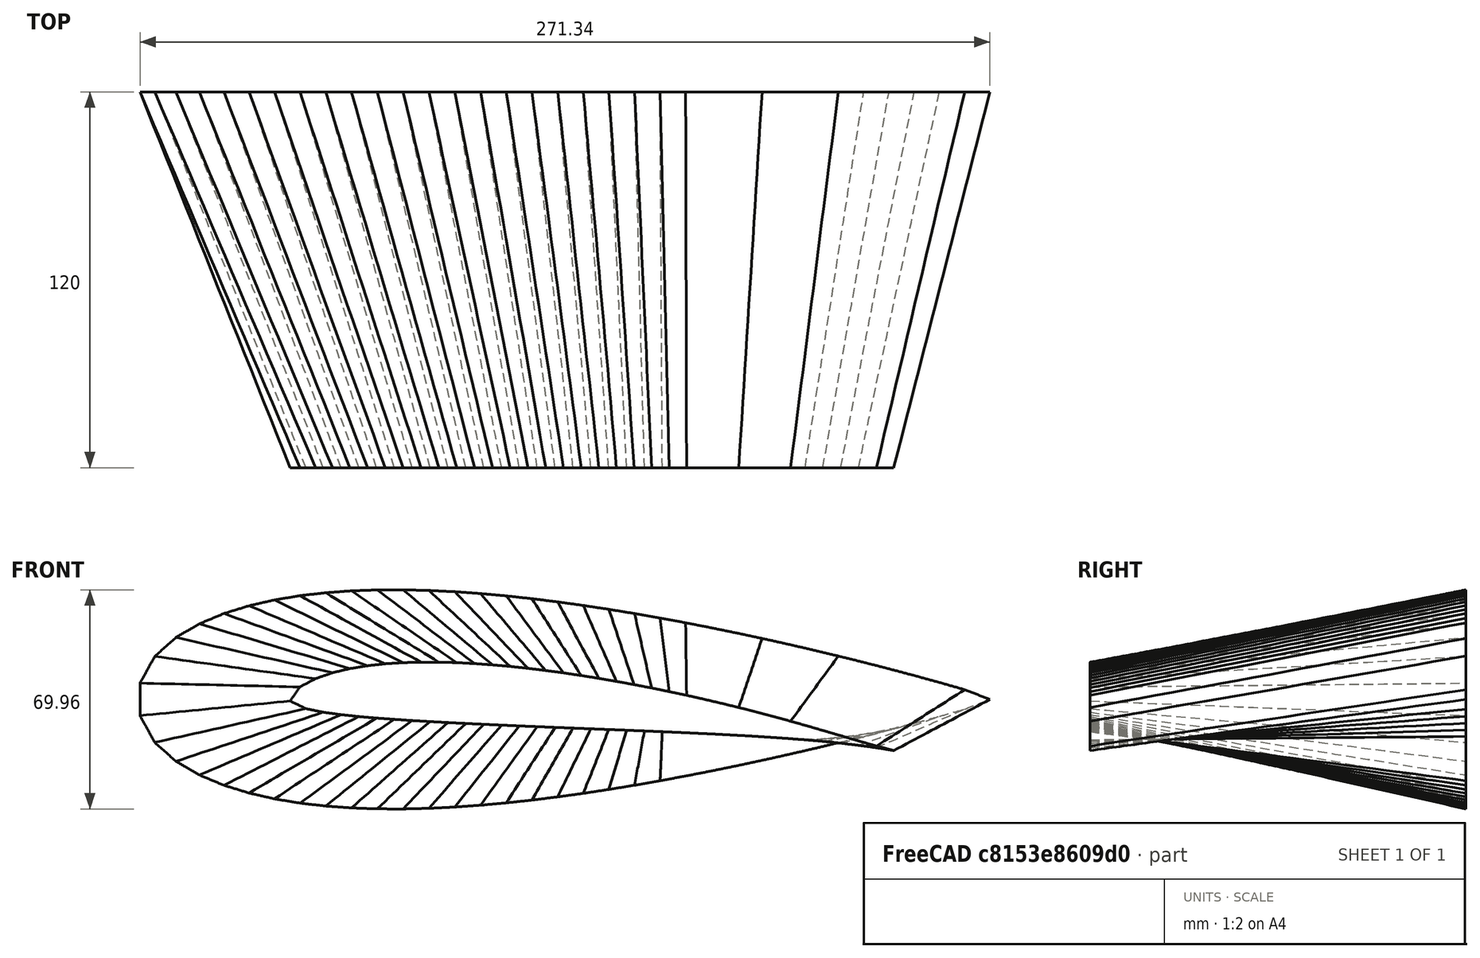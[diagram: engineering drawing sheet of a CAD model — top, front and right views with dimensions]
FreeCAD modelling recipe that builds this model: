
FCSTD DOCUMENT  (FreeCAD 1.0R39319 (Git))
Label: Body
License: All rights reserved
LicenseURL: https://en.wikipedia.org/wiki/All_rights_reserved
objects: App::DocumentObjectGroup×3, PartDesign::SubShapeBinder×2, Part::FeaturePython×2, Part::Part2DObjectPython×2, Part::Loft×1, Part::Mirroring×1, App::Part×1
note: 8 computed .brp shape members not serialized (recipe doc carries the construction recipe); baked Part::Feature solids carry a one-line shape summary decoded from their .brp
EXTERNAL_REF file=Spreadsheet.FCStd obj=plane

FEATURE [PartDesign::SubShapeBinder] Binder  label="Body Airfoil Binder"
  BindCopyOnChange = 0
  BindMode = 0
  ClaimChildren = false
  Context = -> Part [Binder.]
  Fuse = false
  MakeFace = true
  OffsetFill = false
  OffsetIntersection = false
  OffsetJoinType = 0
  OffsetOpenResult = false
  PartialLoad = false
  Placement = pos=(0,0,0) rot=(-1,0,0;4.71239rad)
  Refine = true
  Relative = true
  Support = -> [naca0020]
  _Version = 2
FEATURE [PartDesign::SubShapeBinder] Binder001  label="Wing Base Binder"
  BindCopyOnChange = 0
  BindMode = 0
  ClaimChildren = false
  Context = -> Part [Binder001.]
  Fuse = false
  MakeFace = true
  OffsetFill = false
  OffsetIntersection = false
  OffsetJoinType = 0
  OffsetOpenResult = false
  PartialLoad = false
  Placement = pos=(0,0,0) rot=(1,0,0;1.5708rad)
  Refine = true
  Relative = true
  Support = -> [sd7032]
  _Version = 2
FEATURE [Part::FeaturePython] Clone001  label="Wing Base Binder001"  # Draft clone (typed FeaturePython)
  AttacherType = Attacher::AttachEngine3D
  AttachmentOffset = pos=(48.5542,0,-120) rot=(0,0,1;-0.084525rad)
  AttachmentSupport = -> [XZ_Plane001]
  Fuse = false
  MapMode = 5
  Objects = -> [Binder001]
  Placement = pos=(48.5542,120,-2.66e-14) rot=(-0.998217,-0.042212,0.042212;4.7106rad)
  Scale = (193.508,193.508,1)
  expr: .AttachmentOffset.Base.x = <<Spreadsheet>>#plane.wing_base_start * <<Spreadsheet>>#plane.body_len * 1000
  expr: .AttachmentOffset.Base.y = 0
  expr: .AttachmentOffset.Base.z = -<<Spreadsheet>>#plane.body_span * 1000
  expr: .AttachmentOffset.Rotation.Angle = -1 * <<Spreadsheet>>#plane.attack_angle
  expr: .Placement.Base.x = <<Spreadsheet>>#plane.body_len * <<Spreadsheet>>#plane.wing_base_start * 1000
  expr: .Placement.Base.y = <<Spreadsheet>>#plane.body_span * 1000
  expr: .Placement.Base.z = <<Spreadsheet>>#plane.wing_lift * 1000 * <<Spreadsheet>>#plane.body_height
  expr: .Scale.x = <<Spreadsheet>>#plane.wing_chord * 1000
  expr: .Scale.y = <<Spreadsheet>>#plane.wing_chord * 1000 * <<Spreadsheet>>#plane.scale_y_wing_base
FEATURE [Part::FeaturePython] Clone  label="Body Airfoil Draft"  # Draft clone (typed FeaturePython)
  AttacherType = Attacher::AttachEngine3D
  Fuse = false
  Objects = -> [Binder]
  Placement = pos=(0,0,0) rot=(-1,0,0;4.71239rad)
  Scale = (272.05,349.916,1)
  expr: .Scale.x = <<Spreadsheet>>#plane.body_len * 1000
  expr: .Scale.y = <<Spreadsheet>>#plane.body_len * 1000 * <<Spreadsheet>>#plane.scale_y_body
FEATURE [Part::Part2DObjectPython] Wire  # Draft 2D object (typed FeaturePython)
  Area = 0.136678
  ChamferSize = 0
  Closed = true
  End = (0.970479,-0.00888,0)
  FilletRadius = 0
  Length = 2.08959
  MakeFace = true
  Points = (69) [(1,0,0),(0.970479,0.00888,0),(0.940907,0.015433,0),(0.911288,0.02177,0),(0.881625,0.027901,0),(0.851923,0.033832,0),(0.822181,0.039569,0),+62 more]
  Start = (1,0,0)
  Subdivisions = 0
FEATURE [App::DocumentObjectGroup] naca0020
  Group = -> [Wire]
FEATURE [Part::Part2DObjectPython] Wire001  # Draft 2D object (typed FeaturePython)
  Area = 0.0641761
  ChamferSize = 0
  Closed = true
  End = (0.970594,0.002256,0)
  FilletRadius = 0
  Length = 2.03286
  MakeFace = true
  Points = (69) [(1,0,0),(0.970931,0.004971,0),(0.941994,0.010676,0),(0.913096,0.016568,0),(0.884197,0.022463,0),(0.855281,0.028266,0),(0.826327,0.033885,0),+62 more]
  Start = (1,0,0)
  Subdivisions = 0
FEATURE [App::DocumentObjectGroup] sd7032
  Group = -> [Wire001]
FEATURE [App::DocumentObjectGroup] Group001  label="Airfoils Low Poly"
  Group = -> [naca0020,sd7032]
FEATURE [Part::Loft] Loft
  Closed = false
  MaxDegree = 5
  Ruled = false
  Sections = -> [Clone001,Clone]
  Solid = true
FEATURE [Part::Mirroring] Part__Mirroring  label="Loft (Mirror #1)"
  Base = (0,0,0)
  Normal = (0,1,0)
  Source = -> Loft
FEATURE [App::Part] Part
  Group = -> [Group001,Binder,Clone,Binder001,Clone001,Loft,Part__Mirroring,Wire,naca0020,Wire001,sd7032]
  Origin = -> Origin001
